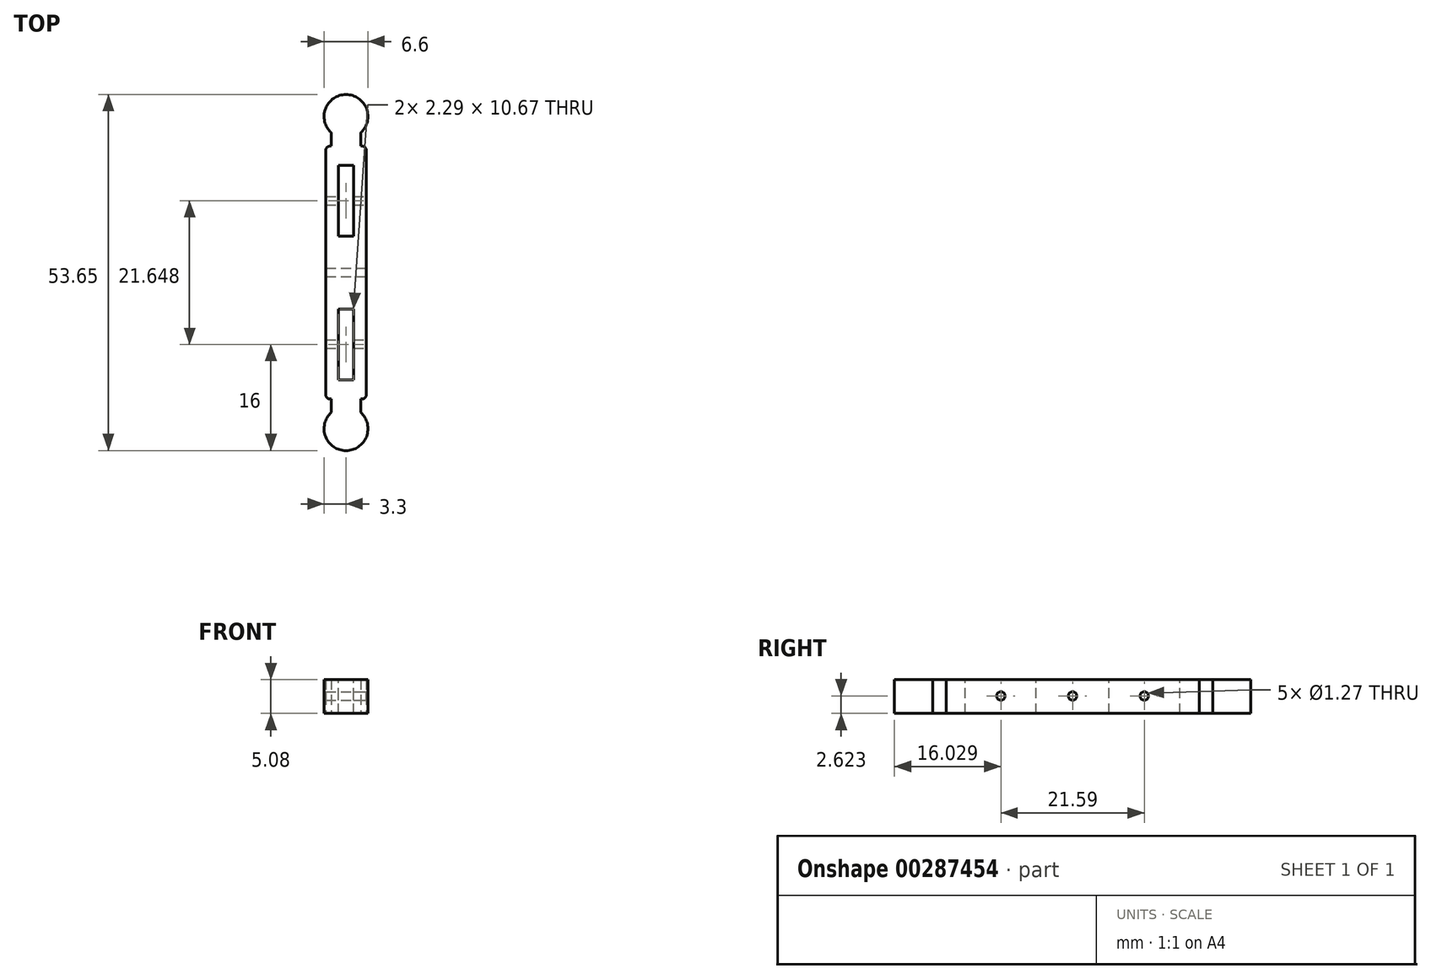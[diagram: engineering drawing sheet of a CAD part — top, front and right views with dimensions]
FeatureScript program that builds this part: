
annotation { "Feature Type Name" : "Feature", "Feature Type Description" : "" }
export const myFeature = defineFeature(function(context is Context, id is Id, definition is map)
    precondition{}
    {
        {
            var Q0;
            Q0=qCreatedBy(makeId("Top.planeOp"),FACE);
            var sketch = newSketch(context, id + "F0", { "sketchPlane" : qUnion([Q0])});
            skCircle(sketch, "E0", {"center": v(0, 0) * mm, "radius": 3.3 * mm});
            skSolve(sketch);
        }
        {
            var Q0;
            Q0=qSketchRegion(id+"F0",true);
            extrude(context, id + "F1", {"entities" : qUnion([Q0]), "depth" : 5.08 * mm});
        }
        {
            var Q0;
            Q0=makeQuery(id+"F1.opExtrude","CAP_FACE",FACE,{"disambiguationData":[OSD([sQuery(id+"F0.wireOp",EDGE,"E0")])],"isStart":true});
            var sketch = newSketch(context, id + "F2", { "sketchPlane" : qUnion([Q0])});
            skLineSegment(sketch, "E1.bottom", {"start": v(-2.22, -2.44) * mm, "end": v(2.22, -2.44) * mm});
            skLineSegment(sketch, "E1.top", {"start": v(-2.22, -4.47) * mm, "end": v(2.22, -4.47) * mm});
            skLineSegment(sketch, "E1.left", {"start": v(-2.22, -2.44) * mm, "end": v(-2.22, -4.47) * mm});
            skLineSegment(sketch, "E1.right", {"start": v(2.22, -2.44) * mm, "end": v(2.22, -4.47) * mm});
            skSolve(sketch);
        }
        {
            var Q0;
            Q0=makeQuery(id+"F2.imprint","IMPRINT",FACE,{"disambiguationData":[TD([[makeQuery(id+"F2.imprint","IMPRINT",EDGE,{"derivedFrom":sQuery(id+"F2.wireOp",EDGE,"E1.top")}),1.0]])]});
            var Q1;
            Q1=makeQuery(id+"F1.opExtrude","CAP_FACE",FACE,{"disambiguationData":[OSD([sQuery(id+"F0.wireOp",EDGE,"E0")])],"isStart":false});
            extrude(context, id + "F3", {"entities" : qUnion([Q0]), "operationType" : NewBodyOperationType.ADD, "endBound" : BoundingType.UP_TO_SURFACE, "oppositeDirection" : true, "endBoundEntityFace" : qUnion([Q1]), "depth" : 25.4 * mm});
        }
        {
            var Q0;
            Q0=qCreatedBy(makeId("Top.planeOp"),FACE);
            var sketch = newSketch(context, id + "F4", { "sketchPlane" : qUnion([Q0])});
            skLineSegment(sketch, "E2.bottom", {"start": v(-3.05, 4.47) * mm, "end": v(3.05, 4.47) * mm});
            skLineSegment(sketch, "E2.top", {"start": v(-3.05, 23.52) * mm, "end": v(3.05, 23.52) * mm});
            skLineSegment(sketch, "E2.left", {"start": v(-3.05, 4.47) * mm, "end": v(-3.05, 23.52) * mm});
            skLineSegment(sketch, "E2.right", {"start": v(3.05, 4.47) * mm, "end": v(3.05, 23.52) * mm});
            skSolve(sketch);
        }
        {
            var Q0;
            Q0=qSketchRegion(id+"F4",true);
            var Q1;
            {var subQ0=sQuery(id+"F0.wireOp",EDGE,"E0");Q1=makeQuery(id+"F3.boolean.opBoolean","MERGE",FACE,{"derivedFrom":[makeQuery(id+"F1.opExtrude","CAP_FACE",FACE,{"disambiguationData":[OSD([subQ0])],"isStart":false}),makeQuery(id+"F3.opExtrude","CAP_FACE",FACE,{"disambiguationData":[OSD([subQ0])],"isStart":false})]});}
            extrude(context, id + "F5", {"entities" : qUnion([Q0]), "operationType" : NewBodyOperationType.ADD, "endBound" : BoundingType.UP_TO_SURFACE, "endBoundEntityFace" : qUnion([Q1]), "depth" : 25.4 * mm});
        }
        {
            var Q0;
            Q0=makeQuery(id+"F5.opExtrude","SWEPT_EDGE",EDGE,{"disambiguationData":[OSD([sQuery(id+"F4.wireOp",EDGE,"E2.bottom"),sQuery(id+"F4.wireOp",EDGE,"E2.right")])]});
            var Q1;
            Q1=makeQuery(id+"F5.opExtrude","SWEPT_EDGE",EDGE,{"disambiguationData":[OSD([sQuery(id+"F4.wireOp",EDGE,"E2.bottom"),sQuery(id+"F4.wireOp",EDGE,"E2.left")])]});
            fillet(context, id + "F6", {"entities" : qUnion([Q0, Q1]), "radius" : 0.64 * mm, "tangentPropagation" : true, "allowEdgeOverflow" : false});
        }
        {
            var Q0;
            {var subQ0=sQuery(id+"F0.wireOp",EDGE,"E0");Q0=makeQuery(id+"F5.boolean.opBoolean","MERGE",FACE,{"derivedFrom":[makeQuery(id+"F3.boolean.opBoolean","MERGE",FACE,{"derivedFrom":[makeQuery(id+"F1.opExtrude","CAP_FACE",FACE,{"disambiguationData":[OSD([subQ0])],"isStart":false}),makeQuery(id+"F3.opExtrude","CAP_FACE",FACE,{"disambiguationData":[OSD([subQ0])],"isStart":false})]}),makeQuery(id+"F5.opExtrude","CAP_FACE",FACE,{"disambiguationData":[OSD([subQ0])],"isStart":false})]});}
            var sketch = newSketch(context, id + "F7", { "sketchPlane" : qUnion([Q0])});
            skLineSegment(sketch, "E3.bottom", {"start": v(1.14, 7.37) * mm, "end": v(-1.14, 7.37) * mm});
            skLineSegment(sketch, "E3.top", {"start": v(1.14, 18.03) * mm, "end": v(-1.14, 18.03) * mm});
            skLineSegment(sketch, "E3.left", {"start": v(1.14, 7.37) * mm, "end": v(1.14, 18.03) * mm});
            skLineSegment(sketch, "E3.right", {"start": v(-1.14, 7.37) * mm, "end": v(-1.14, 18.03) * mm});
            skPoint(sketch, "E3.middle", {"position": v(0, 12.7) * mm});
            skSolve(sketch);
        }
        {
            var Q0;
            Q0=makeQuery(id+"F7.imprint","IMPRINT",FACE,{"disambiguationData":[TD([[makeQuery(id+"F7.imprint","IMPRINT",EDGE,{"derivedFrom":sQuery(id+"F7.wireOp",EDGE,"E3.bottom")}),-1.0]])]});
            extrude(context, id + "F8", {"entities" : qUnion([Q0]), "operationType" : NewBodyOperationType.REMOVE, "oppositeDirection" : true, "depth" : 25.4 * mm});
        }
        {
            var Q0;
            Q0=makeQuery(id+"F1.opExtrude","SWEPT_BODY",BODY,{"disambiguationData":[OSD([sQuery(id+"F0.wireOp",EDGE,"E0")])]});
            var Q1;
            Q1=makeQuery(id+"F5.opExtrude","SWEPT_FACE",FACE,{"disambiguationData":[OSD([sQuery(id+"F4.wireOp",EDGE,"E2.top")])]});
            mirror(context, id + "F9", {"operationType" : NewBodyOperationType.ADD, "entities" : qUnion([Q0]), "mirrorPlane" : qUnion([Q1])});
        }
        {
            var Q0;
            {var subQ0=makeQuery(id+"F5.opExtrude","SWEPT_FACE",FACE,{"disambiguationData":[OSD([sQuery(id+"F4.wireOp",EDGE,"E2.right")])]});Q0=makeQuery(id+"F9.boolean.opBoolean","MERGE",FACE,{"derivedFrom":[subQ0,makeQuery(id+"F9.opPattern","COPY",FACE,{"derivedFrom":subQ0,"instanceName":"1"})]});}
            var sketch = newSketch(context, id + "F10", { "sketchPlane" : qUnion([Q0])});
            skPoint(sketch, "E4", {"position": v(12.73, 2.62) * mm});
            skPoint(sketch, "E5", {"position": v(23.52, 2.62) * mm});
            skPoint(sketch, "E6", {"position": v(34.32, 2.62) * mm});
            skSolve(sketch);
        }
        {
            var Q0;
            Q0=sQuery(id+"F10.wireOp",VERTEX,"E4");
            var Q1;
            Q1=sQuery(id+"F10.wireOp",VERTEX,"E5");
            var Q2;
            Q2=sQuery(id+"F10.wireOp",VERTEX,"E6");
            var Q3;
            Q3=makeQuery(id+"F1.opExtrude","SWEPT_BODY",BODY,{"disambiguationData":[OSD([sQuery(id+"F0.wireOp",EDGE,"E0")])]});
            hole(context, id + "F11", {"style" : HoleStyle.SIMPLE, "endStyle" : HoleEndStyle.THROUGH, "holeDiameter" : 1.27 * mm, "tappedDepth" : 12.7 * mm, "tapClearance" : 3, "startFromSketch" : true, "locations" : qUnion([Q0, Q1, Q2]), "scope" : qUnion([Q3])});
        }
    });
